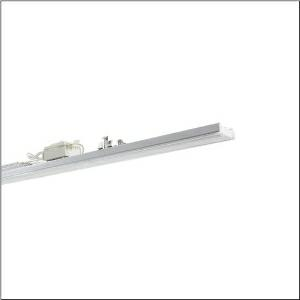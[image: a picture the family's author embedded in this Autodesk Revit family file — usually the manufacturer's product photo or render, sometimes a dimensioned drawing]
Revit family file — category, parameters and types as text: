
# Revit family: licross_r__11_recessed_ho_51te1ecn4cxs_7c7a
name_source: partatom
category: Lighting Fixtures
units: mm (PartAtom-declared; Revit-internal decimal feet)

## family parameters
Cut with Voids When Loaded = No
Host = Face
Light Source = No
Part Type = Normal
Room Calculation Point = No
Round Connector Dimension = Use Diameter
Shared = No

## types (1)
- --- (1 x LED, 12420 lm, 66.5 W, 4000K)
    Apparent Load = 67 VA
    CIE Flux Codes = 85 95 99 100 100
    Color Rendering = 80
    Color Temperature = 4000K
    Default Elevation = 1800 mm
    Description = Licross® 11 Recessed HO, luminaire insert, of sheet steel, galvanised, coil coated, white, length: 1.500mm, width: 66mm, height: 67mm, LED rated luminous flux: 12.420lm, light colour: 840, control gear: ON/OFF Multilumen, CLOi, with plug, 3-pole, with phase selection, mains connection: 220..240V, AC, 50/60Hz, start of lifetime: 67W, end of service life: 75W, internal wiring halogen-free, primary light control with lens, of plastic, primary optical cover: cover, of PMMA, light emission: direct distribution, primary light characteristic: symmetric, protection rating (complete): IP54, insulation class (complete): insulation class I (protective earthing), certification: CE, ENEC, VDE, UKCA, protection symbol: D if used in an environment with non-conductive dust loads with corresponding accessories, impact resistance: IK06, permissible ambient temperature for indoor applications: -35..+35°C, corresponds to IFS (International Featured Standards) requirements for safety and quality in the food industry, reducing of maximum allowable ambient temperature of 5°C with ceiling mounting, LABS conformity tested according to VDMA 24364:2018-05, packaging unit: 1 piece
    Height = 58 mm
    Lamp = 1 x LED
    Lamp Light Flux = 12420 lm
    Lamp Power = 66.5 W
    Lamp count = 1
    Length = 1500 mm
    Luminous efficacy = 187 lm/W
    Manufacturer = Siteco
    ModVariant = No
    Model = 51TE1ECN4CXS
    Mounting Place = Ceiling
    Mounting Type = Pendant
    Number of Poles = 1
    OnlyDefault = Yes
    Power Factor = 1
    Product Name = Licross® 11 Recessed HO
    Product group = luminaire insert | ceiling pendant
    ProductGroupID = 902
    Protection Class = Protection class I
    Protection Degree = IP 54
    RLX_Detail_Level = 1
    RLX_Emergency_Light_Flux = 0 lm
    RLX_Emergency_Type = 0
    RLX_Emergency_Type_DB = No
    RlxData = <blob elided: 22449 chars, md5=27179800>
    Socket = socket
    Standby Power = 0 W
    System Light Flux = 12420 lm
    System Power = 67 W
    Type Comments = factory setting: luminous flux: 100 % | (A | C | E) | 156 mA
    Type Image = l_1296930.jpg
    URL = http://relux.com
    VarID = @adj_105727
    Voltage = 0 V
    Weight = 0.00 kg
    Width = 66 mm

## geometry (parser evidence)
native form markers: Blend x4, Sweep x9
no freeform markers — native parametric forms only
